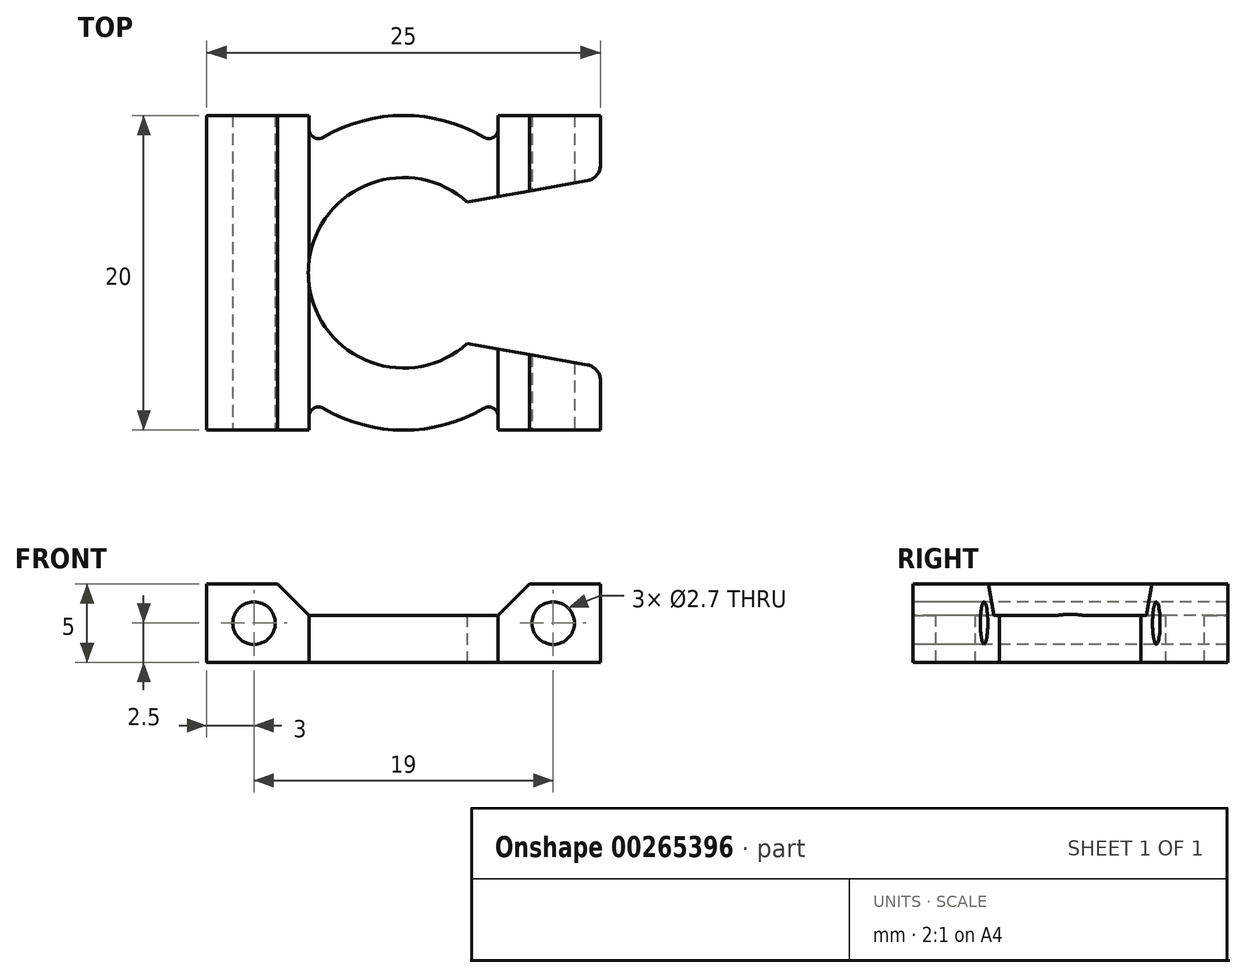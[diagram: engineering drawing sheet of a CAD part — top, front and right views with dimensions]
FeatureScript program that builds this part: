
annotation { "Feature Type Name" : "Feature", "Feature Type Description" : "" }
export const myFeature = defineFeature(function(context is Context, id is Id, definition is map)
    precondition{}
    {
        {
            var Q0;
            Q0=qCreatedBy(makeId("Top.planeOp"),FACE);
            var sketch = newSketch(context, id + "F0", { "sketchPlane" : qUnion([Q0])});
            skArc(sketch, "E0", {"start": v(4.04, 4.5) * mm, "mid": v(-6.05, 0) * mm, "end": v(4.04, -4.5) * mm});
            skLineSegment(sketch, "E1.left", {"start": v(9.5, 10) * mm, "end": v(9.5, -10) * mm, "construction": true});
            skLineSegment(sketch, "E1.right", {"start": v(-9.5, 10) * mm, "end": v(-9.5, -10) * mm, "construction": true});
            skLineSegment(sketch, "E2.bottom", {"start": v(12.5, 10) * mm, "end": v(-12.5, 10) * mm});
            skLineSegment(sketch, "E2.top", {"start": v(12.5, -10) * mm, "end": v(-12.5, -10) * mm});
            skLineSegment(sketch, "E2.right", {"start": v(-12.5, 10) * mm, "end": v(-12.5, -10) * mm});
            skLineSegment(sketch, "E3.0", {"start": v(-8, 10) * mm, "end": v(-8, -10) * mm});
            skLineSegment(sketch, "E4.0", {"start": v(8, 10) * mm, "end": v(8, 5.2) * mm});
            skLineSegment(sketch, "E5.MirrorCS", {"start": v(-11, 10) * mm, "end": v(-11, -10) * mm});
            skLineSegment(sketch, "E6.MirrorCS", {"start": v(11, 10) * mm, "end": v(11, 5.73) * mm});
            skLineSegment(sketch, "E7", {"start": v(12.5, 10) * mm, "end": v(12.5, 6.84) * mm});
            skLineSegment(sketch, "E8", {"start": v(12.5, -10) * mm, "end": v(12.5, -6.84) * mm});
            skPoint(sketch, "E9", {"position": v(4.04, 4.5) * mm});
            skPoint(sketch, "E10", {"position": v(4.04, -4.5) * mm});
            skLineSegment(sketch, "E11", {"start": v(4.04, 4.5) * mm, "end": v(11.67, 5.85) * mm});
            skLineSegment(sketch, "E12", {"start": v(4.04, -4.5) * mm, "end": v(11.67, -5.85) * mm});
            skLineSegment(sketch, "E13.trimOffspring", {"start": v(8, -5.2) * mm, "end": v(8, -10) * mm});
            skLineSegment(sketch, "E14.trimOffspring", {"start": v(11, -5.73) * mm, "end": v(11, -10) * mm});
            skPoint(sketch, "E15.visualSharp", {"position": v(12.5, 6) * mm});
            skArc(sketch, "E15.filletArc", {"start": v(11.67, 5.85) * mm, "mid": v(12.27, 6.2) * mm, "end": v(12.5, 6.84) * mm});
            skPoint(sketch, "E16.visualSharp", {"position": v(12.5, -6) * mm});
            skArc(sketch, "E16.filletArc", {"start": v(12.5, -6.84) * mm, "mid": v(12.27, -6.2) * mm, "end": v(11.67, -5.85) * mm});
            skSolve(sketch);
        }
        {
            var Q0;
            {var subQ4=sQuery(id+"F0.wireOp",EDGE,"E0");Q0=makeQuery(id+"F0.imprint","IMPRINT",FACE,{"disambiguationData":[TD([[makeQuery(id+"F0.imprint","IMPRINT",EDGE,{"derivedFrom":subQ4}),-1.0]])]});}
            var Q1;
            {var subQ0=sQuery(id+"F0.wireOp",EDGE,"E4.0");Q1=makeQuery(id+"F0.imprint","IMPRINT",FACE,{"disambiguationData":[TD([[makeQuery(id+"F0.imprint","IMPRINT",EDGE,{"derivedFrom":subQ0}),1.0]])]});}
            var Q2;
            {var subQ1=sQuery(id+"F0.wireOp",EDGE,"E6.MirrorCS");Q2=makeQuery(id+"F0.imprint","IMPRINT",FACE,{"disambiguationData":[TD([[makeQuery(id+"F0.imprint","IMPRINT",EDGE,{"derivedFrom":subQ1}),1.0]])]});}
            var Q3;
            {var subQ3=sQuery(id+"F0.wireOp",EDGE,"E8");Q3=makeQuery(id+"F0.imprint","IMPRINT",FACE,{"disambiguationData":[TD([[makeQuery(id+"F0.imprint","IMPRINT",EDGE,{"derivedFrom":subQ3}),1.0]])]});}
            var Q4;
            {var subQ0=sQuery(id+"F0.wireOp",EDGE,"E13.trimOffspring");Q4=makeQuery(id+"F0.imprint","IMPRINT",FACE,{"disambiguationData":[TD([[makeQuery(id+"F0.imprint","IMPRINT",EDGE,{"derivedFrom":subQ0}),1.0]])]});}
            var Q5;
            {var subQ0=sQuery(id+"F0.wireOp",EDGE,"E2.right");Q5=makeQuery(id+"F0.imprint","IMPRINT",FACE,{"disambiguationData":[TD([[makeQuery(id+"F0.imprint","IMPRINT",EDGE,{"derivedFrom":subQ0}),1.0]])]});}
            var Q6;
            {var subQ0=sQuery(id+"F0.wireOp",EDGE,"E3.0");Q6=makeQuery(id+"F0.imprint","IMPRINT",FACE,{"disambiguationData":[TD([[makeQuery(id+"F0.imprint","IMPRINT",EDGE,{"derivedFrom":subQ0}),-1.0]])]});}
            extrude(context, id + "F1", {"entities" : qUnion([Q0, Q1, Q2, Q3, Q4, Q5, Q6]), "depth" : 5 * mm});
        }
        {
            var Q0;
            Q0=makeQuery(id+"F1.opExtrude","SWEPT_FACE",FACE,{"disambiguationData":[OSD([sQuery(id+"F0.wireOp",EDGE,"E2.top")])]});
            var sketch = newSketch(context, id + "F2", { "sketchPlane" : qUnion([Q0])});
            skPoint(sketch, "E17.0", {"position": v(-9.5, 0) * mm});
            skPoint(sketch, "E17.1", {"position": v(9.5, 0) * mm});
            skLineSegment(sketch, "E18", {"start": v(-9.5, 0) * mm, "end": v(-9.5, 5) * mm, "construction": true});
            skLineSegment(sketch, "E19", {"start": v(9.5, 0) * mm, "end": v(9.5, 5) * mm, "construction": true});
            skCircle(sketch, "E20", {"center": v(-9.5, 2.5) * mm, "radius": 1.35 * mm});
            skCircle(sketch, "E21", {"center": v(9.5, 2.5) * mm, "radius": 1.35 * mm});
            skPoint(sketch, "E22.0", {"position": v(0, 0) * mm});
            skLineSegment(sketch, "E23", {"start": v(0, 0) * mm, "end": v(0, 5) * mm, "construction": true});
            skLineSegment(sketch, "E24", {"start": v(0, 5) * mm, "end": v(8, 5) * mm});
            skLineSegment(sketch, "E25", {"start": v(0, 3) * mm, "end": v(6, 3) * mm});
            skLineSegment(sketch, "E26", {"start": v(6, 3) * mm, "end": v(8, 5) * mm});
            skLineSegment(sketch, "E27.MirrorCS", {"start": v(0, 3) * mm, "end": v(-6, 3) * mm});
            skLineSegment(sketch, "E28.MirrorCS", {"start": v(-6, 3) * mm, "end": v(-8, 5) * mm});
            skLineSegment(sketch, "E29.MirrorCS", {"start": v(0, 5) * mm, "end": v(-8, 5) * mm});
            skSolve(sketch);
        }
        {
            var Q0;
            Q0=makeQuery(id+"F2.imprint","IMPRINT",FACE,{"disambiguationData":[TD([[makeQuery(id+"F2.imprint","IMPRINT",EDGE,{"derivedFrom":sQuery(id+"F2.wireOp",EDGE,"E20")}),1.0]])]});
            var Q1;
            Q1=makeQuery(id+"F2.imprint","IMPRINT",FACE,{"disambiguationData":[TD([[makeQuery(id+"F2.imprint","IMPRINT",EDGE,{"derivedFrom":sQuery(id+"F2.wireOp",EDGE,"E21")}),1.0]])]});
            var Q2;
            Q2=makeQuery(id+"F2.imprint","IMPRINT",FACE,{"disambiguationData":[TD([[makeQuery(id+"F2.imprint","IMPRINT",EDGE,{"derivedFrom":sQuery(id+"F2.wireOp",EDGE,"E24")}),1.0]])]});
            extrude(context, id + "F3", {"entities" : qUnion([Q0, Q1, Q2]), "operationType" : NewBodyOperationType.REMOVE, "oppositeDirection" : true, "depth" : 25 * mm});
        }
        {
            var Q0;
            Q0=makeQuery(id+"F3.boolean.opBoolean","COPY",FACE,{"disambiguationData":[TD([makeQuery(id+"F1.opExtrude","SWEPT_FACE",FACE,{"disambiguationData":[OSD([sQuery(id+"F0.wireOp",EDGE,"E2.bottom")])]})])],"derivedFrom":makeQuery(id+"F3.opExtrude","SWEPT_FACE",FACE,{"disambiguationData":[OSD([sQuery(id+"F2.wireOp",EDGE,"E25"),sQuery(id+"F2.wireOp",EDGE,"E27.MirrorCS")])]})});
            var sketch = newSketch(context, id + "F4", { "sketchPlane" : qUnion([Q0])});
            skArc(sketch, "E30", {"start": v(6, 8) * mm, "mid": v(0, 10) * mm, "end": v(-6, 8) * mm});
            skLineSegment(sketch, "E31", {"start": v(-6, 10) * mm, "end": v(-6, 8) * mm});
            skLineSegment(sketch, "E32", {"start": v(-6, 10) * mm, "end": v(6, 10) * mm});
            skLineSegment(sketch, "E33", {"start": v(6, 10) * mm, "end": v(6, 8) * mm});
            skLineSegment(sketch, "E34", {"start": v(-6.19, 0) * mm, "end": v(5.8, 0) * mm, "construction": true});
            skLineSegment(sketch, "E35.MirrorCS", {"start": v(6, -10) * mm, "end": v(6, -8) * mm});
            skLineSegment(sketch, "E36.MirrorCS", {"start": v(-6, -10) * mm, "end": v(-6, -8) * mm});
            skLineSegment(sketch, "E37.MirrorCS", {"start": v(-6, -10) * mm, "end": v(6, -10) * mm});
            skArc(sketch, "E38.MirrorCS", {"start": v(6, -8) * mm, "mid": v(0, -10) * mm, "end": v(-6, -8) * mm});
            skSolve(sketch);
        }
        {
            var Q0;
            {var subQ0=sQuery(id+"F4.wireOp",EDGE,"E33");Q0=makeQuery(id+"F4.imprint","IMPRINT",FACE,{"disambiguationData":[TD([[makeQuery(id+"F4.imprint","IMPRINT",EDGE,{"derivedFrom":subQ0}),-1.0]])]});}
            var Q1;
            {var subQ0=sQuery(id+"F4.wireOp",EDGE,"E31");Q1=makeQuery(id+"F4.imprint","IMPRINT",FACE,{"disambiguationData":[TD([[makeQuery(id+"F4.imprint","IMPRINT",EDGE,{"derivedFrom":subQ0}),1.0]])]});}
            var Q2;
            {var subQ0=sQuery(id+"F4.wireOp",EDGE,"E36.MirrorCS");Q2=makeQuery(id+"F4.imprint","IMPRINT",FACE,{"disambiguationData":[TD([[makeQuery(id+"F4.imprint","IMPRINT",EDGE,{"derivedFrom":subQ0}),-1.0]])]});}
            var Q3;
            {var subQ0=sQuery(id+"F4.wireOp",EDGE,"E35.MirrorCS");Q3=makeQuery(id+"F4.imprint","IMPRINT",FACE,{"disambiguationData":[TD([[makeQuery(id+"F4.imprint","IMPRINT",EDGE,{"derivedFrom":subQ0}),1.0]])]});}
            extrude(context, id + "F5", {"entities" : qUnion([Q0, Q1, Q2, Q3]), "operationType" : NewBodyOperationType.REMOVE, "oppositeDirection" : true, "depth" : 25 * mm});
        }
        {
            var Q0;
            Q0=makeQuery(id+"F5.boolean.opBoolean","COPY",EDGE,{"derivedFrom":makeQuery(id+"F5.opExtrude","SWEPT_EDGE",EDGE,{"disambiguationData":[OSD([sQuery(id+"F4.wireOp",EDGE,"E36.MirrorCS"),sQuery(id+"F4.wireOp",EDGE,"E38.MirrorCS")])]})});
            var Q1;
            Q1=makeQuery(id+"F5.boolean.opBoolean","COPY",EDGE,{"derivedFrom":makeQuery(id+"F5.opExtrude","SWEPT_EDGE",EDGE,{"disambiguationData":[OSD([sQuery(id+"F2.wireOp",EDGE,"E27.MirrorCS"),sQuery(id+"F2.wireOp",EDGE,"E28.MirrorCS"),sQuery(id+"F4.wireOp",EDGE,"E30"),sQuery(id+"F4.wireOp",EDGE,"E31")])]})});
            var Q2;
            Q2=makeQuery(id+"F5.boolean.opBoolean","COPY",EDGE,{"derivedFrom":makeQuery(id+"F5.opExtrude","SWEPT_EDGE",EDGE,{"disambiguationData":[OSD([sQuery(id+"F2.wireOp",EDGE,"E25"),sQuery(id+"F2.wireOp",EDGE,"E26"),sQuery(id+"F4.wireOp",EDGE,"E30"),sQuery(id+"F4.wireOp",EDGE,"E33")])]})});
            var Q3;
            Q3=makeQuery(id+"F5.boolean.opBoolean","COPY",EDGE,{"derivedFrom":makeQuery(id+"F5.opExtrude","SWEPT_EDGE",EDGE,{"disambiguationData":[OSD([sQuery(id+"F4.wireOp",EDGE,"E35.MirrorCS"),sQuery(id+"F4.wireOp",EDGE,"E38.MirrorCS")])]})});
            fillet(context, id + "F6", {"entities" : qUnion([Q0, Q1, Q2, Q3]), "radius" : 0.6 * mm, "tangentPropagation" : true, "allowEdgeOverflow" : false});
        }
    });
